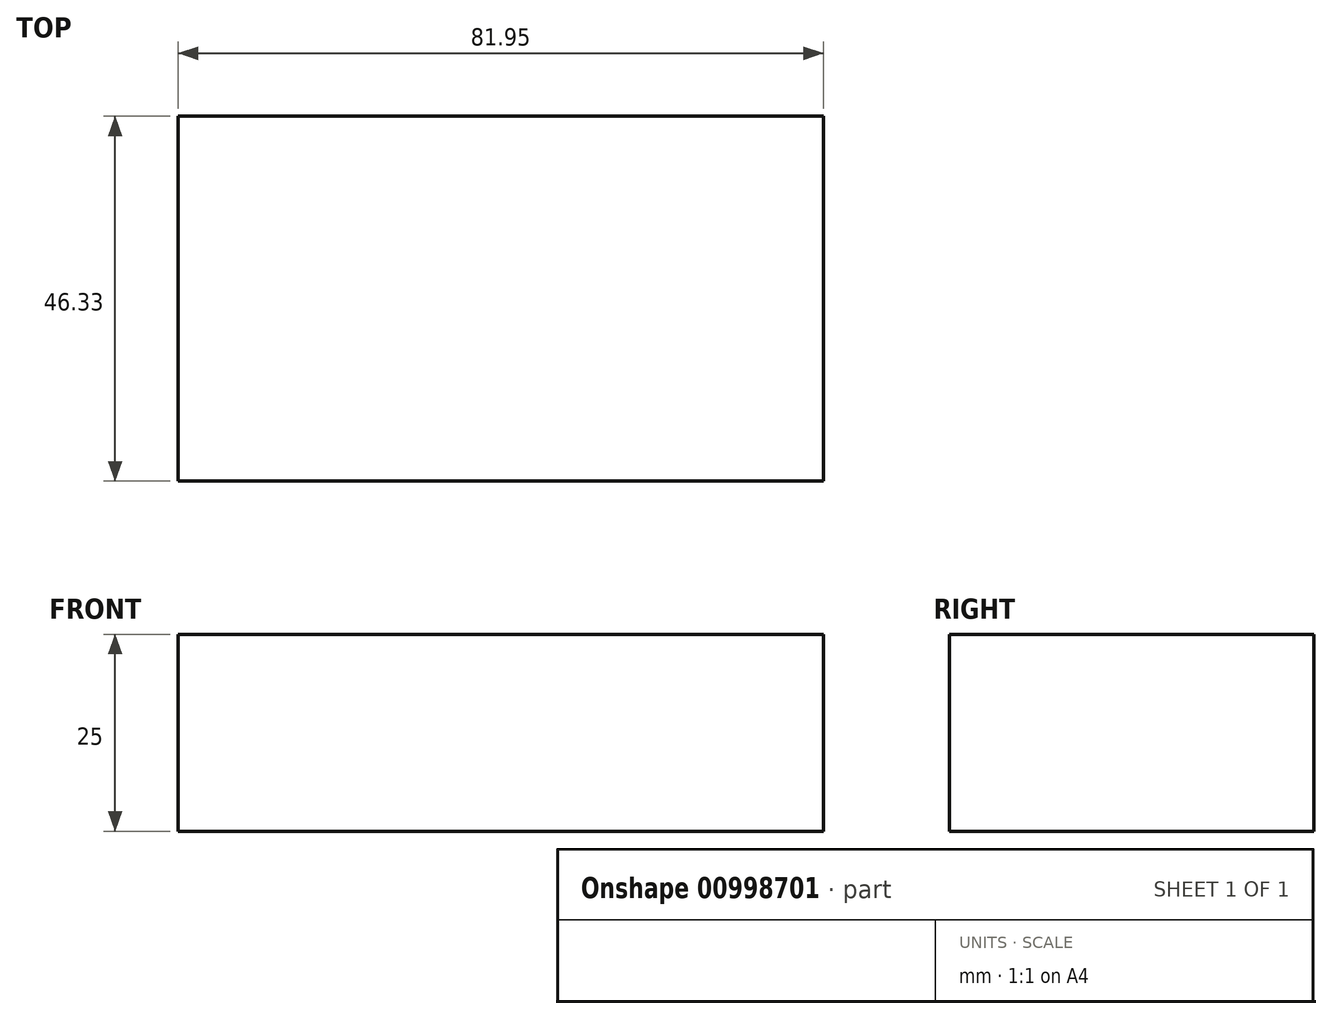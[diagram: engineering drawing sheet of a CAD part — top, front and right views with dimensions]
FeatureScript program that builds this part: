
annotation { "Feature Type Name" : "Feature", "Feature Type Description" : "" }
export const myFeature = defineFeature(function(context is Context, id is Id, definition is map)
    precondition{}
    {
        {
            var Q0;
            Q0=qCreatedBy(makeId("Top.planeOp"),FACE);
            var sketch = newSketch(context, id + "F0", { "sketchPlane" : qUnion([Q0])});
            skLineSegment(sketch, "E0.bottom", {"start": v(36.56, 0) * mm, "end": v(-45.39, 0) * mm});
            skLineSegment(sketch, "E0.top", {"start": v(36.56, 46.33) * mm, "end": v(-45.39, 46.33) * mm});
            skLineSegment(sketch, "E0.left", {"start": v(36.56, 0) * mm, "end": v(36.56, 46.33) * mm});
            skLineSegment(sketch, "E0.right", {"start": v(-45.39, 0) * mm, "end": v(-45.39, 46.33) * mm});
            skSolve(sketch);
        }
        {
            var Q0;
            Q0 = qSketchRegion(id + "F0", true);
            var Q1;
            Q1=makeQuery(id+"F0.imprint","IMPRINT",FACE,{"disambiguationData":[TD([[makeQuery(id+"F0.imprint","IMPRINT",EDGE,{"derivedFrom":sQuery(id+"F0.wireOp",EDGE,"E0.bottom")}),-1.0]])]});
            extrude(context, id + "F1", {"entities" : qUnion([Q0, Q1]), "depth" : 25 * mm, "offsetDistance" : 25 * mm});
        }
    });
